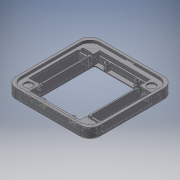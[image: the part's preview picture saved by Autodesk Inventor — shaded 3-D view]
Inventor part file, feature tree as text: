
AUTODESK INVENTOR PART (.ipt)
format: ipt  version: 2016 SP2 (Build 200236200, 236)  size: 443,392 bytes
history: native  units: mm
features: extrude x11, sketch x11, fillet x1, chamfer x1
ambient origin geometry x8: Origin, YZ Plane, XZ Plane, XY Plane, X Axis, Y Axis, Z Axis, Center Point
bodies: Volumenkörper1 (feature_tree)
feature tree (24):
  extrude  "Extrusion1"  Depth=70.3mm
  extrude  "Extrusion2"  Depth=5.0mm
  extrude  "Extrusion7"  Depth=10.5mm
  extrude  "Extrusion8"  Depth=48.8mm
  extrude  "Extrusion9"  Depth=1.2mm
  extrude  "Extrusion10"  Depth=0.8mm
  extrude  "Extrusion12"  Depth=3.0mm
  extrude  "Extrusion13"  Depth=2.0mm
  extrude  "Extrusion14"  Depth=0.5mm
  extrude  "Extrusion15"  Depth=0.8mm
  fillet  "Rundung1"  Radius=0.5mm
  chamfer  "Fase3"  Distance=3.75mm
  extrude  "Extrusion17"  Depth=2.0mm
  sketch  "Skizze1"  dims[d0=50.3mm d1=70.3mm]
  sketch  "Skizze2"  dims[d2=5.0mm d3=5.0mm]
  sketch  "Skizze7"  dims[d4=10.5mm d5=10.5mm]
  sketch  "Skizze8"  dims[d6=48.8mm d7=48.8mm]
  sketch  "Skizze9"  dims[d8=1.2mm d9=1.2mm]
  sketch  "Skizze10"  dims[d11=0.8mm d12=0.8mm]
  sketch  "Skizze12"  dims[d13=0.8mm d14=3.0mm]
  sketch  "Skizze13"  dims[d15=3.75mm d16=2.0mm]
  sketch  "Skizze14"  dims[d17=3.0mm d18=0.5mm]
  sketch  "Skizze15"  dims[d19=0.5mm d20=0.8mm d21=0.5mm d22=0.5mm]
  sketch  "Skizze17"  dims[d23=3.0mm d26=3.75mm d27=2.0mm d28=0.5mm d30=3.0mm d31=0.8mm d32=0.8mm d33=1.6mm d34=1.0mm d35=1.0mm d36=3.0mm d37=3.0mm d38=1.0mm d39=1.0mm d40=1.6mm d41=10.0mm d42=0.0mm d43=5.6mm d44=59.0mm d45=2.0mm d46=0.8mm d47=0.0mm d80=8.15mm d81=8.15mm d82=6.0mm d83=6.0mm d84=6.0mm d85=6.0mm d86=1.4mm d87=0.0mm d88=3.0mm d89=3.0mm d90=3.8mm d91=0.0mm d92=3.0mm d93=3.0mm d94=3.8mm d95=0.0mm d96=8.5mm d97=0.5mm d98=0.5mm d99=2.0mm d100=0.5mm d101=2.0mm d102=0.5mm d103=1.6mm d104=8.5mm d105=2.0mm d106=0.5mm d107=1.5mm d108=0.0mm d122=2.6mm d123=0.0mm d124=1.9mm d125=0.6mm d126=5.2mm d127=1.0mm d128=5.2mm d129=1.0mm d130=1.2mm d131=0.0mm d132=4.1mm d133=1.0mm d134=8.2mm d135=1.2mm d136=0.0mm d137=10.8mm d138=0.0mm d139=10.0mm d140=5.3mm d141=1.2mm d142=6.108652mm d147=1.35mm d148=1.35mm d149=3.0mm d150=2.85mm d151=5.0mm d152=5.0mm d153=5.0mm d154=2.85mm d155=10.15mm d156=10.15mm d157=2.85mm d158=10.15mm d159=10.15mm d160=2.85mm d161=3.0mm d162=5.0mm d163=3.0mm d164=3.0mm d165=6.0mm d166=0.0mm]
